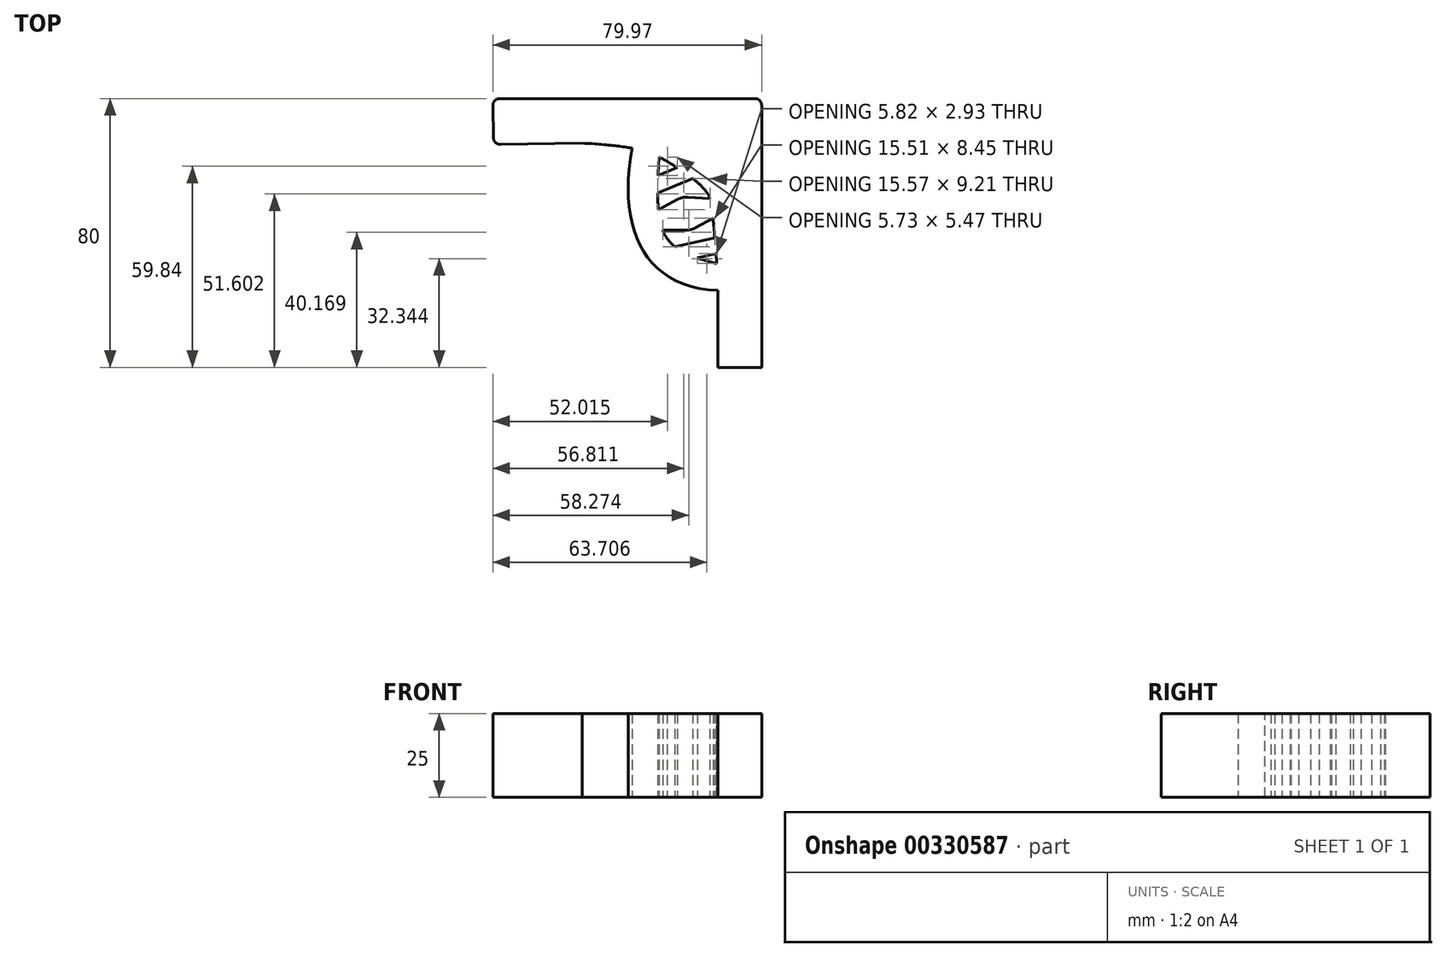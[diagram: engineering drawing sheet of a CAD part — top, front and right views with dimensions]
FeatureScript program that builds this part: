
annotation { "Feature Type Name" : "Feature", "Feature Type Description" : "" }
export const myFeature = defineFeature(function(context is Context, id is Id, definition is map)
    precondition{}
    {
        {
            var Q0;
            Q0=qCreatedBy(makeId("Top.planeOp"),FACE);
            var sketch = newSketch(context, id + "F0", { "sketchPlane" : qUnion([Q0])});
            skLineSegment(sketch, "E0", {"start": v(0, -2) * mm, "end": v(0, -80) * mm});
            skLineSegment(sketch, "E1", {"start": v(0, -80) * mm, "end": v(-13, -80) * mm});
            skLineSegment(sketch, "E2", {"start": v(-79.82, -11.7) * mm, "end": v(-79.97, -2.03) * mm});
            skLineSegment(sketch, "E3", {"start": v(-77.97, 0) * mm, "end": v(-2, 0) * mm});
            skPoint(sketch, "E4.visualSharp", {"position": v(0, 0) * mm});
            skArc(sketch, "E4.filletArc", {"start": v(0, -2) * mm, "mid": v(-0.59, -0.59) * mm, "end": v(-2, 0) * mm});
            skLineSegment(sketch, "E5", {"start": v(-79.97, -2.03) * mm, "end": v(-79.82, -11.7) * mm});
            skPoint(sketch, "E6.visualSharp", {"position": v(-80, 0) * mm});
            skArc(sketch, "E6.filletArc", {"start": v(-77.97, 0) * mm, "mid": v(-79.4, -0.6) * mm, "end": v(-79.97, -2.03) * mm});
            skLineSegment(sketch, "E7", {"start": v(-77.8, -13.66) * mm, "end": v(-53.42, -13.3) * mm});
            skPoint(sketch, "E8.visualSharp", {"position": v(-79.8, -13.7) * mm});
            skArc(sketch, "E8.filletArc", {"start": v(-79.82, -11.7) * mm, "mid": v(-79.22, -13.1) * mm, "end": v(-77.8, -13.66) * mm});
            skLineSegment(sketch, "E9", {"start": v(-13, -80) * mm, "end": v(-13, -69.7) * mm});
            skLineSegment(sketch, "E10", {"start": v(-13.05, -57.12) * mm, "end": v(-13.36, -49.12) * mm});
            skFitSpline(sketch, "E11", {"points": [v(-38.54, -14.79) * mm, v(-34.93, -45.81) * mm, v(-13.05, -57.12) * mm], "startDerivative": vector(-13.43, -73.7) * mm, "endDerivative": vector(66.92, -2.03) * mm});
            skFitSpline(sketch, "E12", {"points": [v(-30.54, -17.43) * mm, v(-28.1, -41.66) * mm, v(-13.36, -49.12) * mm], "startDerivative": vector(-2.7, -51.5) * mm, "endDerivative": vector(38.66, -10.44) * mm});
            skFitSpline(sketch, "E13", {"points": [v(-53.42, -13.3) * mm, v(-38.54, -14.79) * mm, v(-30.54, -17.43) * mm, v(-16.92, -27.13) * mm, v(-14.58, -34.15) * mm, v(-13.36, -49.12) * mm, v(-13.05, -57.12) * mm, v(-13, -69.7) * mm], "startDerivative": vector(105.03, -4.05) * mm, "endDerivative": vector(0.4, -92.66) * mm});
            skFitSpline(sketch, "E14", {"points": [v(-30.29, -36.23) * mm, v(-28.1, -41.66) * mm], "startDerivative": vector(2.2, -5.42) * mm, "endDerivative": vector(5, -6.1) * mm});
            skLineSegment(sketch, "E15", {"start": v(-30.29, -36.03) * mm, "end": v(-27.24, -30.6) * mm});
            skLineSegment(sketch, "E16", {"start": v(-23.6, -28.09) * mm, "end": v(-16.92, -27.13) * mm});
            skLineSegment(sketch, "E17", {"start": v(-28.1, -41.66) * mm, "end": v(-21.77, -41) * mm});
            skLineSegment(sketch, "E18", {"start": v(-18.3, -39.05) * mm, "end": v(-14.58, -34.15) * mm});
            skPoint(sketch, "E19.visualSharp", {"position": v(-26.04, -28.44) * mm});
            skArc(sketch, "E19.filletArc", {"start": v(-23.6, -28.09) * mm, "mid": v(-25.7, -28.92) * mm, "end": v(-27.24, -30.6) * mm});
            skPoint(sketch, "E20.visualSharp", {"position": v(-19.6, -40.79) * mm});
            skArc(sketch, "E20.filletArc", {"start": v(-21.77, -41) * mm, "mid": v(-19.83, -40.4) * mm, "end": v(-18.3, -39.05) * mm});
            skSolve(sketch);
        }
        {
            var Q0;
            Q0 = qSketchRegion(id + "F0", true);
            extrude(context, id + "F1", {"entities" : qUnion([Q0]), "depth" : 25 * mm});
        }
        {
            var Q0;
            Q0=qCreatedBy(makeId("Top.planeOp"),FACE);
            var sketch = newSketch(context, id + "F2", { "sketchPlane" : qUnion([Q0])});
            skLineSegment(sketch, "E21", {"start": v(-32, -33.68) * mm, "end": v(-25.09, -30.04) * mm});
            skLineSegment(sketch, "E22", {"start": v(-21.95, -29.35) * mm, "end": v(-13.27, -29.84) * mm});
            skPoint(sketch, "E23.visualSharp", {"position": v(-23.62, -29.26) * mm});
            skArc(sketch, "E23.filletArc", {"start": v(-21.95, -29.35) * mm, "mid": v(-23.57, -29.48) * mm, "end": v(-25.09, -30.04) * mm});
            skPoint(sketch, "E24.visualSharp", {"position": v(-18.48, -43.08) * mm});
            skArc(sketch, "E24.filletArc", {"start": v(-19.54, -43.08) * mm, "mid": v(-18.5, -42.98) * mm, "end": v(-17.48, -42.71) * mm});
            skLineSegment(sketch, "E25", {"start": v(-23.37, -19.85) * mm, "end": v(-32.83, -23.71) * mm});
            skLineSegment(sketch, "E26", {"start": v(-32.83, -23.71) * mm, "end": v(-31.03, -28.1) * mm});
            skLineSegment(sketch, "E27", {"start": v(-31.03, -28.1) * mm, "end": v(-19.88, -23.54) * mm});
            skLineSegment(sketch, "E28", {"start": v(-19.88, -23.54) * mm, "end": v(-23.37, -19.85) * mm});
            skLineSegment(sketch, "E29", {"start": v(-26.99, -44.3) * mm, "end": v(-11.7, -40.9) * mm});
            skLineSegment(sketch, "E30", {"start": v(-11.7, -40.9) * mm, "end": v(-9.74, -45.34) * mm});
            skLineSegment(sketch, "E31", {"start": v(-9.74, -45.34) * mm, "end": v(-25.54, -48.85) * mm});
            skLineSegment(sketch, "E32", {"start": v(-25.54, -48.85) * mm, "end": v(-26.99, -44.3) * mm});
            skLineSegment(sketch, "E33", {"start": v(-32, -33.68) * mm, "end": v(-30.86, -39.17) * mm});
            skLineSegment(sketch, "E34", {"start": v(-30.86, -39.17) * mm, "end": v(-22.49, -39.17) * mm});
            skLineSegment(sketch, "E35", {"start": v(-19.6, -38.43) * mm, "end": v(-12.43, -34.5) * mm});
            skLineSegment(sketch, "E36", {"start": v(-12.43, -34.5) * mm, "end": v(-13.27, -29.84) * mm});
            skPoint(sketch, "E37.visualSharp", {"position": v(-20.95, -39.17) * mm});
            skArc(sketch, "E37.filletArc", {"start": v(-22.49, -39.17) * mm, "mid": v(-21, -38.98) * mm, "end": v(-19.6, -38.43) * mm});
            skSolve(sketch);
        }
        {
            var Q0;
            Q0 = qSketchRegion(id + "F2", true);
            extrude(context, id + "F3", {"entities" : qUnion([Q0]), "operationType" : NewBodyOperationType.ADD, "depth" : 25 * mm});
        }
    });
